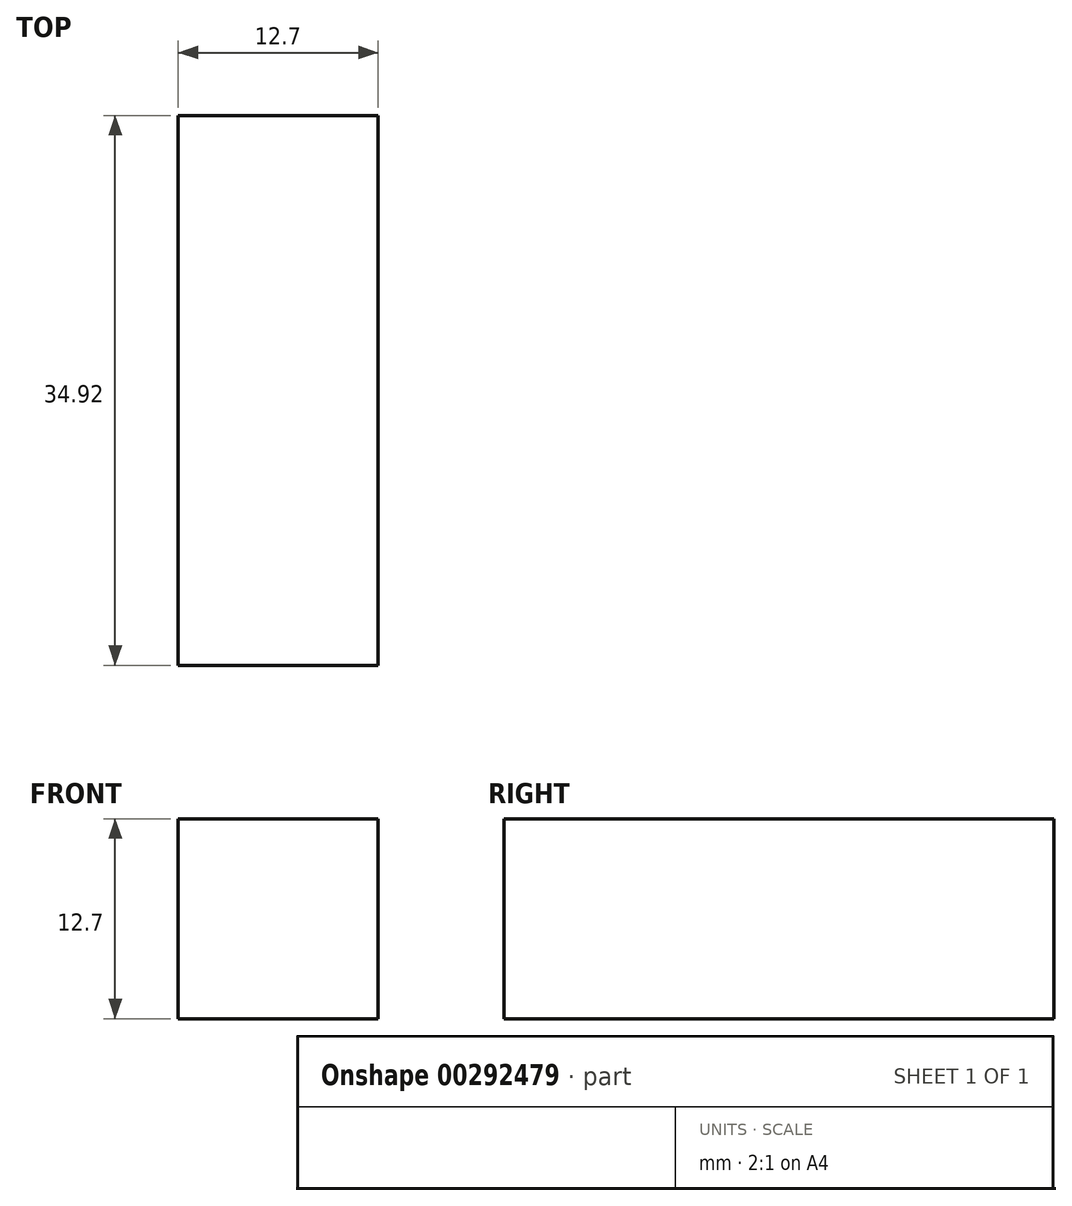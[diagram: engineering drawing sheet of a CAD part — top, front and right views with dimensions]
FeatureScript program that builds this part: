
annotation { "Feature Type Name" : "Feature", "Feature Type Description" : "" }
export const myFeature = defineFeature(function(context is Context, id is Id, definition is map)
    precondition{}
    {
        {
            var Q0;
            Q0=qCreatedBy(makeId("Front.planeOp"),FACE);
            var sketch = newSketch(context, id + "F0", { "sketchPlane" : qUnion([Q0])});
            skLineSegment(sketch, "E0.bottom", {"start": v(-6.35, 6.35) * mm, "end": v(6.35, 6.35) * mm});
            skLineSegment(sketch, "E0.top", {"start": v(-6.35, -6.35) * mm, "end": v(6.35, -6.35) * mm});
            skLineSegment(sketch, "E0.left", {"start": v(-6.35, 6.35) * mm, "end": v(-6.35, -6.35) * mm});
            skLineSegment(sketch, "E0.right", {"start": v(6.35, 6.35) * mm, "end": v(6.35, -6.35) * mm});
            skSolve(sketch);
        }
        {
            var Q0;
            Q0=makeQuery(id+"F0.imprint","IMPRINT",FACE,{"disambiguationData":[TD([[makeQuery(id+"F0.imprint","IMPRINT",EDGE,{"derivedFrom":sQuery(id+"F0.wireOp",EDGE,"E0.bottom")}),-1.0]])]});
            extrude(context, id + "F1", {"entities" : qUnion([Q0]), "depth" : 34.92 * mm});
        }
    });
